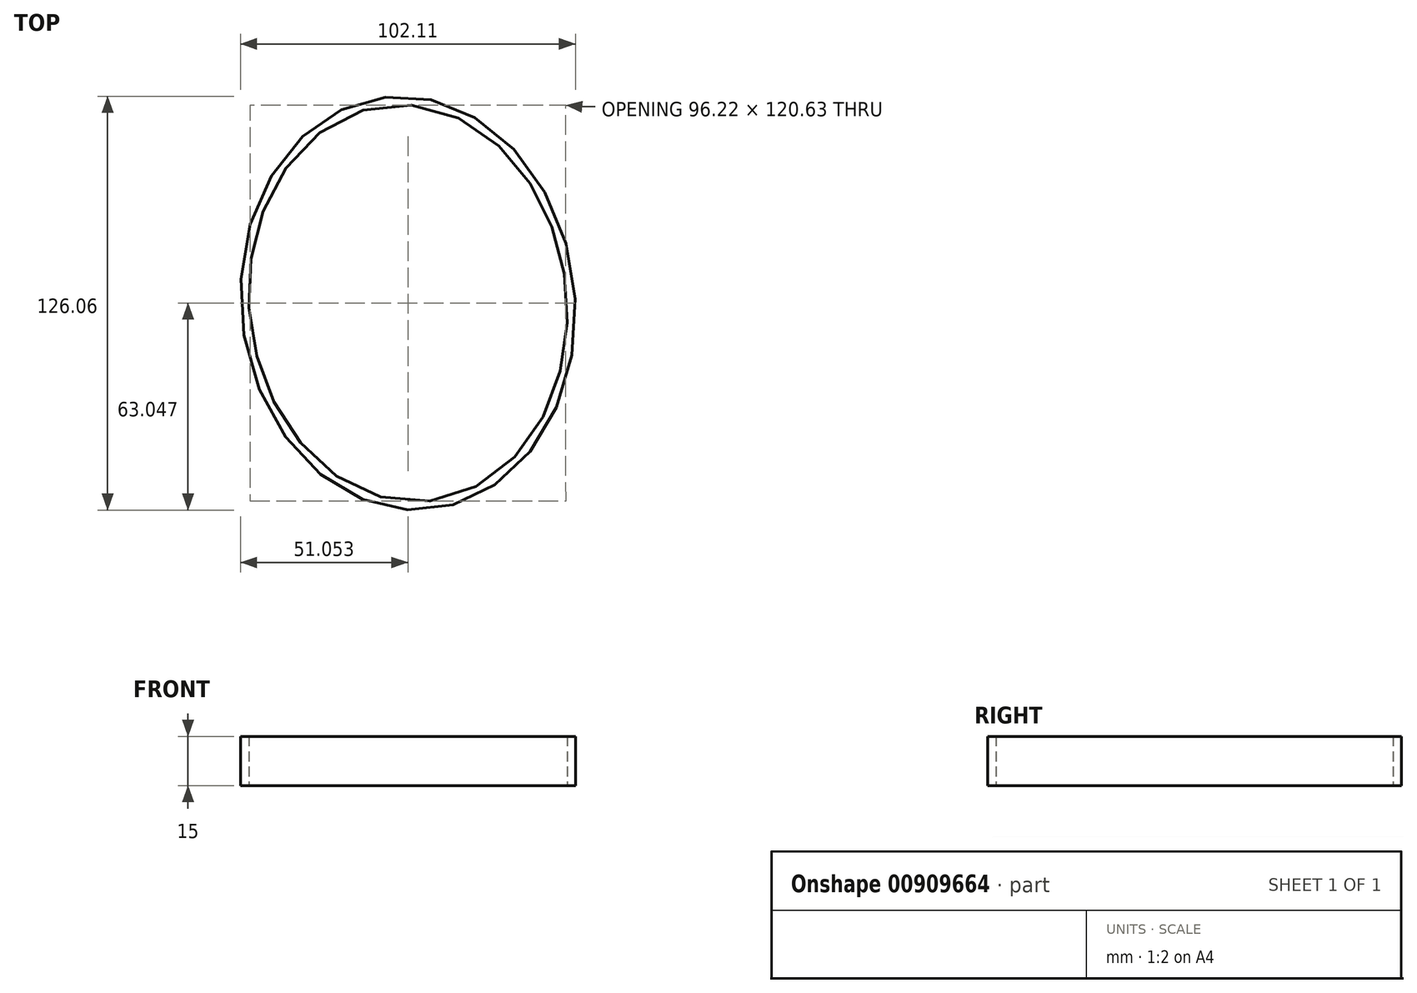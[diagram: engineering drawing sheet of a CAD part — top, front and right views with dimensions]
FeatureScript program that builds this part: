
annotation { "Feature Type Name" : "Feature", "Feature Type Description" : "" }
export const myFeature = defineFeature(function(context is Context, id is Id, definition is map)
    precondition{}
    {
        {
            var Q0;
            Q0=qCreatedBy(makeId("Top.planeOp"),FACE);
            var sketch = newSketch(context, id + "F0", { "sketchPlane" : qUnion([Q0])});
            skEllipse(sketch, "E0", {"center": v(-58.74, -45.49) * mm, "majorRadius": 63.16 * mm, "minorRadius": 50.89 * mm, "majorAxis": v(-0.1, 1)});
            skSolve(sketch);
        }
        {
            var Q0;
            Q0 = qSketchRegion(id + "F0", true);
            extrude(context, id + "F1", {"entities" : qUnion([Q0]), "depth" : 15 * mm, "offsetDistance" : 25 * mm});
        }
        {
            var Q0;
            Q0=makeQuery(id+"F1.opExtrude","CAP_FACE",FACE,{"disambiguationData":[OSD([sQuery(id+"F0.wireOp",EDGE,"E0")])],"isStart":true});
            var Q1;
            Q1=makeQuery(id+"F1.opExtrude","CAP_FACE",FACE,{"disambiguationData":[OSD([sQuery(id+"F0.wireOp",EDGE,"E0")])],"isStart":false});
            shell(context, id + "F2", {"entities" : qUnion([Q0, Q1]), "thickness" : 2.5 * mm});
        }
    });
